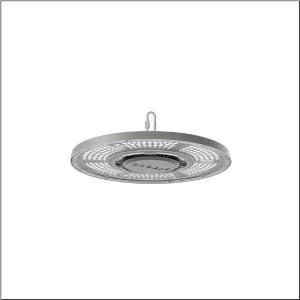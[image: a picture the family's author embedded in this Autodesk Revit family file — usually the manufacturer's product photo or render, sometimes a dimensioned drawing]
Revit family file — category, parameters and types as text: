
# Revit family: highbay_31-s_51hc42da4fmb
name_source: partatom
category: Lighting Fixtures
units: mm (PartAtom-declared; Revit-internal decimal feet)

## family parameters
Cut with Voids When Loaded = No
Host = Face
Light Source = No
Part Type = Normal
Room Calculation Point = No
Round Connector Dimension = Use Diameter
Shared = No

## types (1)
- Highbay 31-S (1 x LED, 14000 lm, 94 W, 4000K)
    Apparent Load = 94 VA
    CIE Flux Codes = 77 99 100 100 100
    Color Rendering = 80
    Color Temperature = 4000K
    Default Elevation = 1800 mm
    Description = Highbay 31-S, LED high bay luminaire, primary light control with lens, of PC, primary optical cover: cover panel, of PC, transparent, light emission: direct distribution, primary light characteristic: rotationally symmetric, installation type: suspended mounting, surface-mounted, LED, rated luminous flux: 14.000lm, luminous efficacy: 150lm/W, light colour: 840, colour temperature: 4000K, control gear: ECG DALI, with cable, 5x 1.0mm², free wire ends, mains connection: 220..240V, AC/DC, 0/50..60Hz, cable length: 1,5m, rated input power: 94W, housing, rotationally symmetric, of diecast aluminium, powder-coated, grey aluminium (RAL 9007), with hook on luminaire side, incl. screw, diameter: 339mm, protection rating (complete): IP65, insulation class (complete): insulation class I (protective earthing), certification: CE, ENEC, UKCA, protection symbol: D, impact resistance: IK08, permissible operating ambient temperature: -30..+45°C, standard: EN 60598-2-22, EN 60598, corresponds to IFS (International Featured Standards) requirements for safety and quality in the food industry, packaging unit: 1 piece
    Height = 141 mm
    Lamp = 1 x LED
    Lamp Light Flux = 14000 lm
    Lamp Power = 94 W
    Lamp count = 1
    Length = 339 mm
    Luminous efficacy = 149 lm/W
    Manufacturer = Siteco
    ModVariant = No
    Model = 51HC42DA4FMB
    Mounting Place = Ceiling
    Mounting Type = Pendant
    Number of Poles = 1
    OnlyDefault = Yes
    Power Factor = 1
    Product Name = Highbay 31-S
    Product group = LED high bay luminaire
    ProductGroupID = 903
    Protection Class = Protection class I
    Protection Degree = IP 65
    RLX_Detail_Level = 1
    RLX_Emergency_Light_Flux = 0 lm
    RLX_Emergency_Type = 0
    RLX_Emergency_Type_DB = No
    RlxData = <blob elided: 162105 chars, md5=4f583997>
    Socket = socket
    Standby Power = 0 W
    System Light Flux = 14000 lm
    System Power = 94 W
    Type Comments = Product without accessories
    Type Image = l_1007237.jpg
    URL = http://relux.com
    VarID = ---
    Voltage = 0 V
    Weight = 0.00 kg
    Width = 0 mm  [stored 0 ft]

note: [stored X ft] marks values corroborated as IEEE doubles in the binary element streams (Revit-internal decimal feet)

## geometry (parser evidence)
native form markers: Blend x4, Sweep x11
no freeform markers — native parametric forms only
